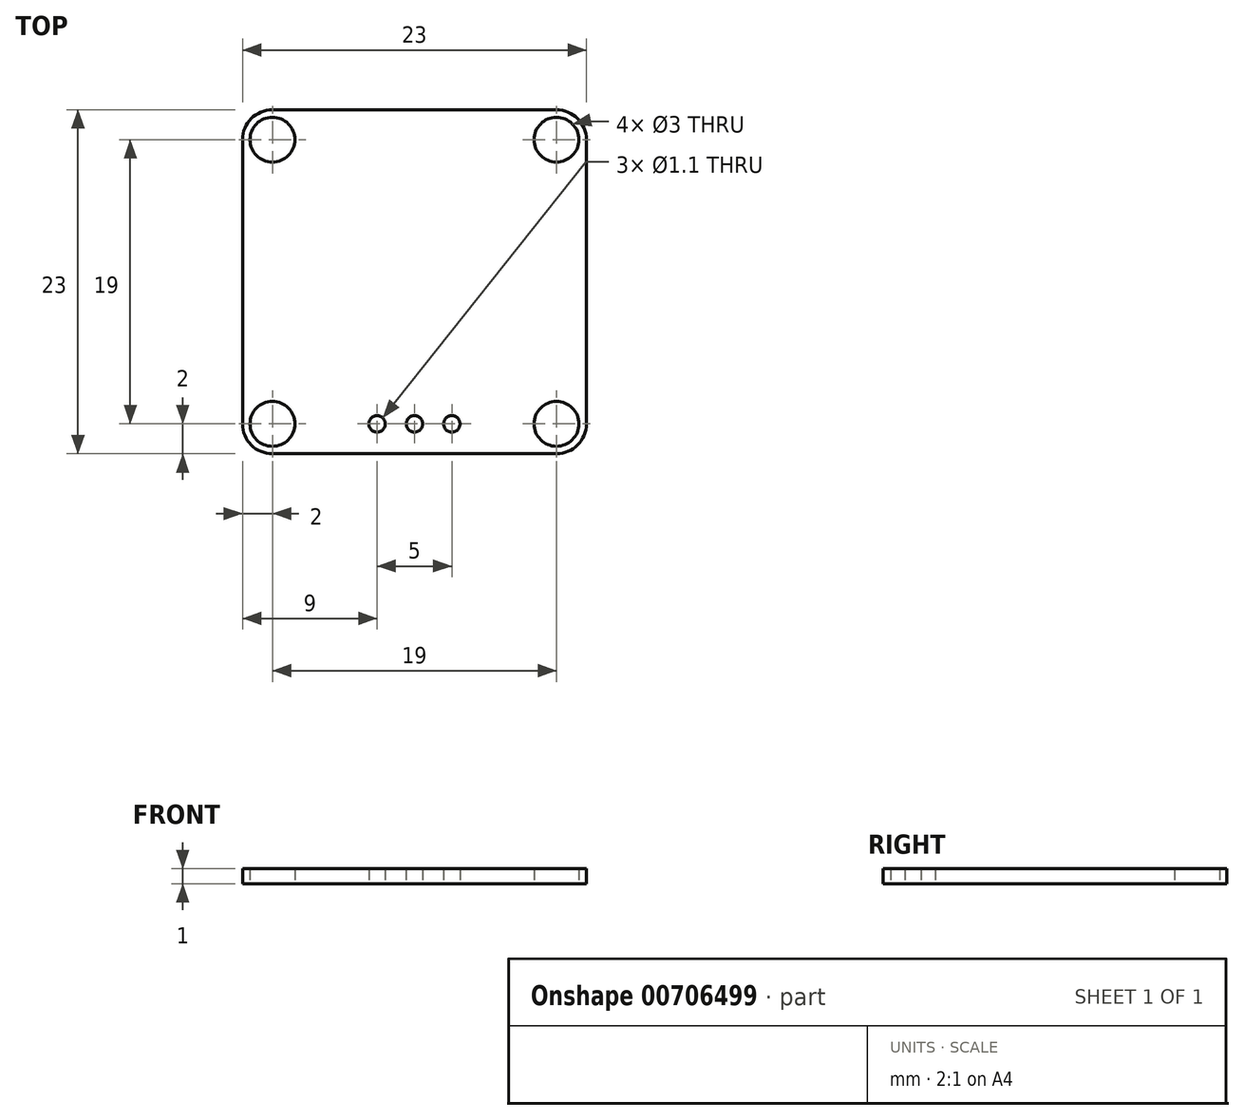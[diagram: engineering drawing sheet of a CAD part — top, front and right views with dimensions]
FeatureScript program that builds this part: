
annotation { "Feature Type Name" : "Feature", "Feature Type Description" : "" }
export const myFeature = defineFeature(function(context is Context, id is Id, definition is map)
    precondition{}
    {
        {
            var Q0;
            Q0=qCreatedBy(makeId("Top.planeOp"),FACE);
            var sketch = newSketch(context, id + "F0", { "sketchPlane" : qUnion([Q0])});
            skLineSegment(sketch, "E0.bottom", {"start": v(9.5, -11.5) * mm, "end": v(-9.5, -11.5) * mm});
            skLineSegment(sketch, "E0.top", {"start": v(9.5, 11.5) * mm, "end": v(-9.5, 11.5) * mm});
            skLineSegment(sketch, "E0.left", {"start": v(11.5, -9.5) * mm, "end": v(11.5, 9.5) * mm});
            skLineSegment(sketch, "E0.right", {"start": v(-11.5, -9.5) * mm, "end": v(-11.5, 9.5) * mm});
            skPoint(sketch, "E0.middle", {"position": v(0, 0) * mm});
            skPoint(sketch, "E1.visualSharp", {"position": v(-11.5, 11.5) * mm});
            skArc(sketch, "E1.filletArc", {"start": v(-9.5, 11.5) * mm, "mid": v(-10.91, 10.91) * mm, "end": v(-11.5, 9.5) * mm});
            skPoint(sketch, "E2.visualSharp", {"position": v(11.5, 11.5) * mm});
            skArc(sketch, "E2.filletArc", {"start": v(11.5, 9.5) * mm, "mid": v(10.91, 10.91) * mm, "end": v(9.5, 11.5) * mm});
            skPoint(sketch, "E3.visualSharp", {"position": v(11.5, -11.5) * mm});
            skArc(sketch, "E3.filletArc", {"start": v(9.5, -11.5) * mm, "mid": v(10.91, -10.91) * mm, "end": v(11.5, -9.5) * mm});
            skPoint(sketch, "E4.visualSharp", {"position": v(-11.5, -11.5) * mm});
            skArc(sketch, "E4.filletArc", {"start": v(-11.5, -9.5) * mm, "mid": v(-10.91, -10.91) * mm, "end": v(-9.5, -11.5) * mm});
            skPoint(sketch, "E5", {"position": v(-2.5, -9.5) * mm});
            skPoint(sketch, "E6.1.0.0", {"position": v(0, -9.5) * mm});
            skPoint(sketch, "E6.2.0.0", {"position": v(2.5, -9.5) * mm});
            skLineSegment(sketch, "E6.direction1", {"start": v(-2.5, -9.5) * mm, "end": v(0, -9.5) * mm, "construction": true});
            skSolve(sketch);
        }
        {
            var Q0;
            Q0=makeQuery(id+"F0.imprint","IMPRINT",FACE,{"disambiguationData":[TD([[makeQuery(id+"F0.imprint","IMPRINT",EDGE,{"derivedFrom":sQuery(id+"F0.wireOp",EDGE,"E0.bottom")}),-1.0]])]});
            extrude(context, id + "F1", {"entities" : qUnion([Q0]), "depth" : 1 * mm, "offsetDistance" : 25 * mm});
        }
        {
            var Q0;
            Q0=sQuery(id+"F0.wireOp",VERTEX,"E1.filletArc.center");
            var Q1;
            Q1=sQuery(id+"F0.wireOp",VERTEX,"E2.filletArc.center");
            var Q2;
            Q2=sQuery(id+"F0.wireOp",VERTEX,"E3.filletArc.center");
            var Q3;
            Q3=sQuery(id+"F0.wireOp",VERTEX,"E4.filletArc.center");
            var Q4;
            Q4=makeQuery(id+"F1.opExtrude","SWEPT_BODY",BODY,{"disambiguationData":[OSD([sQuery(id+"F0.wireOp",EDGE,"E0.bottom"),sQuery(id+"F0.wireOp",EDGE,"E0.top"),sQuery(id+"F0.wireOp",EDGE,"E0.left"),sQuery(id+"F0.wireOp",EDGE,"E0.right"),sQuery(id+"F0.wireOp",EDGE,"E1.filletArc"),sQuery(id+"F0.wireOp",EDGE,"E2.filletArc"),sQuery(id+"F0.wireOp",EDGE,"E3.filletArc"),sQuery(id+"F0.wireOp",EDGE,"E4.filletArc")])]});
            hole(context, id + "F2", {"style" : HoleStyle.SIMPLE, "endStyle" : HoleEndStyle.THROUGH, "oppositeDirection" : true, "holeDiameter" : 3 * mm, "majorDiameter" : 5 * mm, "isTappedThrough" : true, "tappedDepth" : 6 * mm, "tapClearance" : 3, "locations" : qUnion([Q0, Q1, Q2, Q3]), "scope" : qUnion([Q4])});
        }
        {
            var Q0;
            Q0=sQuery(id+"F0.wireOp",VERTEX,"E5");
            var Q1;
            Q1=sQuery(id+"F0.wireOp",VERTEX,"E6.1.0.0");
            var Q2;
            Q2=sQuery(id+"F0.wireOp",VERTEX,"E6.2.0.0");
            var Q3;
            Q3=makeQuery(id+"F1.opExtrude","SWEPT_BODY",BODY,{"disambiguationData":[OSD([sQuery(id+"F0.wireOp",EDGE,"E0.bottom"),sQuery(id+"F0.wireOp",EDGE,"E0.top"),sQuery(id+"F0.wireOp",EDGE,"E0.left"),sQuery(id+"F0.wireOp",EDGE,"E0.right"),sQuery(id+"F0.wireOp",EDGE,"E1.filletArc"),sQuery(id+"F0.wireOp",EDGE,"E2.filletArc"),sQuery(id+"F0.wireOp",EDGE,"E3.filletArc"),sQuery(id+"F0.wireOp",EDGE,"E4.filletArc")])]});
            hole(context, id + "F3", {"style" : HoleStyle.SIMPLE, "endStyle" : HoleEndStyle.THROUGH, "oppositeDirection" : true, "holeDiameter" : 1.1 * mm, "majorDiameter" : 5 * mm, "isTappedThrough" : true, "tappedDepth" : 6 * mm, "tapClearance" : 3, "locations" : qUnion([Q0, Q1, Q2]), "scope" : qUnion([Q3])});
        }
    });
